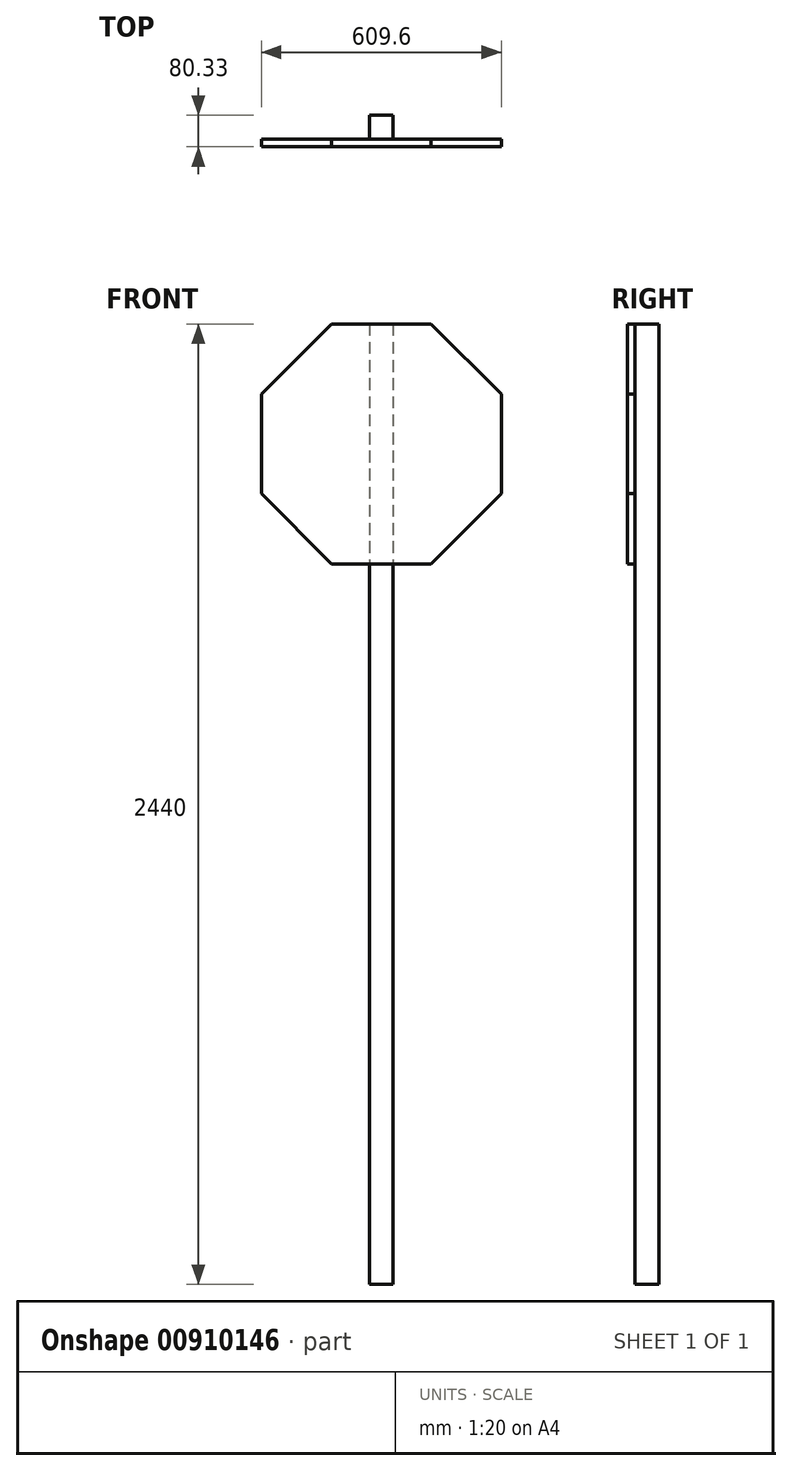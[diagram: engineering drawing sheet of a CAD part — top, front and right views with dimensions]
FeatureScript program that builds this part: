
annotation { "Feature Type Name" : "Feature", "Feature Type Description" : "" }
export const myFeature = defineFeature(function(context is Context, id is Id, definition is map)
    precondition{}
    {
        {
            var Q0;
            Q0=qCreatedBy(makeId("Front.planeOp"),FACE);
            var sketch = newSketch(context, id + "F0", { "sketchPlane" : qUnion([Q0])});
            skLineSegment(sketch, "E0", {"start": v(0, 0) * mm, "end": v(16, 30.4) * mm});
            skLineSegment(sketch, "E1", {"start": v(0, 0) * mm, "end": v(16, 0) * mm});
            skLineSegment(sketch, "E2", {"start": v(16, 0) * mm, "end": v(16, 30.4) * mm});
            skLineSegment(sketch, "E3", {"start": v(0, 0) * mm, "end": v(0.65, 12.48) * mm});
            skLineSegment(sketch, "E4", {"start": v(0.65, 12.48) * mm, "end": v(5.18, 24.13) * mm});
            skLineSegment(sketch, "E5", {"start": v(5.18, 24.13) * mm, "end": v(16, 30.4) * mm});
            skCircle(sketch, "E6", {"center": v(0, 0) * mm, "radius": 37.5 * mm, "construction": true});
            skLineSegment(sketch, "E7", {"start": v(0, 0) * mm, "end": v(-12.5, 0) * mm});
            skLineSegment(sketch, "E8", {"start": v(-12.5, 0) * mm, "end": v(-25, 0) * mm});
            skLineSegment(sketch, "E9", {"start": v(-25, 0) * mm, "end": v(-37.5, 0) * mm});
            skSolve(sketch);
        }
        {
            var Q0;
            Q0=qCreatedBy(makeId("Front.planeOp"),FACE);
            var sketch = newSketch(context, id + "F1", { "sketchPlane" : qUnion([Q0])});
            skLineSegment(sketch, "E10.bottom", {"start": v(-30.16, 1220) * mm, "end": v(30.16, 1220) * mm});
            skLineSegment(sketch, "E10.top", {"start": v(-30.16, -1220) * mm, "end": v(30.16, -1220) * mm});
            skLineSegment(sketch, "E10.left", {"start": v(-30.16, 1220) * mm, "end": v(-30.17, -1220) * mm});
            skLineSegment(sketch, "E10.right", {"start": v(30.17, 1220) * mm, "end": v(30.16, -1220) * mm});
            skLineSegment(sketch, "E11", {"start": v(0, 1220) * mm, "end": v(0, -1220) * mm, "construction": true});
            skCircle(sketch, "E12.cCircle", {"center": v(0, 915.2) * mm, "radius": 304.8 * mm, "construction": true});
            skLineSegment(sketch, "E12.0", {"start": v(126.25, 610.4) * mm, "end": v(-126.25, 610.4) * mm});
            skLineSegment(sketch, "E12.1", {"start": v(-126.25, 610.4) * mm, "end": v(-304.8, 788.95) * mm});
            skLineSegment(sketch, "E12.2", {"start": v(-304.8, 788.95) * mm, "end": v(-304.8, 1041.45) * mm});
            skLineSegment(sketch, "E12.3", {"start": v(-304.8, 1041.45) * mm, "end": v(-126.25, 1220) * mm});
            skLineSegment(sketch, "E12.4", {"start": v(-126.25, 1220) * mm, "end": v(126.25, 1220) * mm});
            skLineSegment(sketch, "E12.5", {"start": v(126.25, 1220) * mm, "end": v(304.8, 1041.45) * mm});
            skLineSegment(sketch, "E12.6", {"start": v(304.8, 1041.45) * mm, "end": v(304.8, 788.95) * mm});
            skLineSegment(sketch, "E12.7", {"start": v(304.8, 788.95) * mm, "end": v(126.25, 610.4) * mm});
            skPoint(sketch, "E12.0.midPoint", {"position": v(0, 610.4) * mm});
            skSolve(sketch);
        }
        {
            var Q0;
            {var subQ0=sQuery(id+"F1.wireOp",EDGE,"E12.4");var subQ1=sQuery(id+"F1.wireOp",EDGE,"E10.left");var subQ2=makeQuery(id+"F1.imprint","INTERSECT",VERTEX,{"derivedFrom":[subQ1,subQ0]});Q0=makeQuery(id+"F1.imprint","IMPRINT",FACE,{"disambiguationData":[TD([[makeQuery(id+"F1.imprint","IMPRINT",EDGE,{"disambiguationData":[TD([[subQ2,-1.0]])],"derivedFrom":subQ1}),1.0]])]});}
            var Q1;
            {var subQ0=sQuery(id+"F1.wireOp",EDGE,"E12.1");Q1=makeQuery(id+"F1.imprint","IMPRINT",FACE,{"disambiguationData":[TD([[makeQuery(id+"F1.imprint","IMPRINT",EDGE,{"derivedFrom":subQ0}),-1.0]])]});}
            var Q2;
            {var subQ0=sQuery(id+"F1.wireOp",EDGE,"E12.5");Q2=makeQuery(id+"F1.imprint","IMPRINT",FACE,{"disambiguationData":[TD([[makeQuery(id+"F1.imprint","IMPRINT",EDGE,{"derivedFrom":subQ0}),-1.0]])]});}
            extrude(context, id + "F2", {"entities" : qUnion([Q0, Q1, Q2]), "depth" : 20 * mm, "offsetDistance" : 25 * mm});
        }
        {
            var Q0;
            {var subQ0=sQuery(id+"F1.wireOp",EDGE,"E10.top");Q0=makeQuery(id+"F1.imprint","IMPRINT",FACE,{"disambiguationData":[TD([[makeQuery(id+"F1.imprint","IMPRINT",EDGE,{"derivedFrom":subQ0}),1.0]])]});}
            var Q1;
            {var subQ0=sQuery(id+"F1.wireOp",EDGE,"E12.4");var subQ1=sQuery(id+"F1.wireOp",EDGE,"E10.left");var subQ2=makeQuery(id+"F1.imprint","INTERSECT",VERTEX,{"derivedFrom":[subQ1,subQ0]});Q1=makeQuery(id+"F1.imprint","IMPRINT",FACE,{"disambiguationData":[TD([[makeQuery(id+"F1.imprint","IMPRINT",EDGE,{"disambiguationData":[TD([[subQ2,-1.0]])],"derivedFrom":subQ1}),1.0]])]});}
            extrude(context, id + "F3", {"entities" : qUnion([Q0, Q1]), "oppositeDirection" : true, "depth" : 60.33 * mm, "offsetDistance" : 25 * mm});
        }
    });
